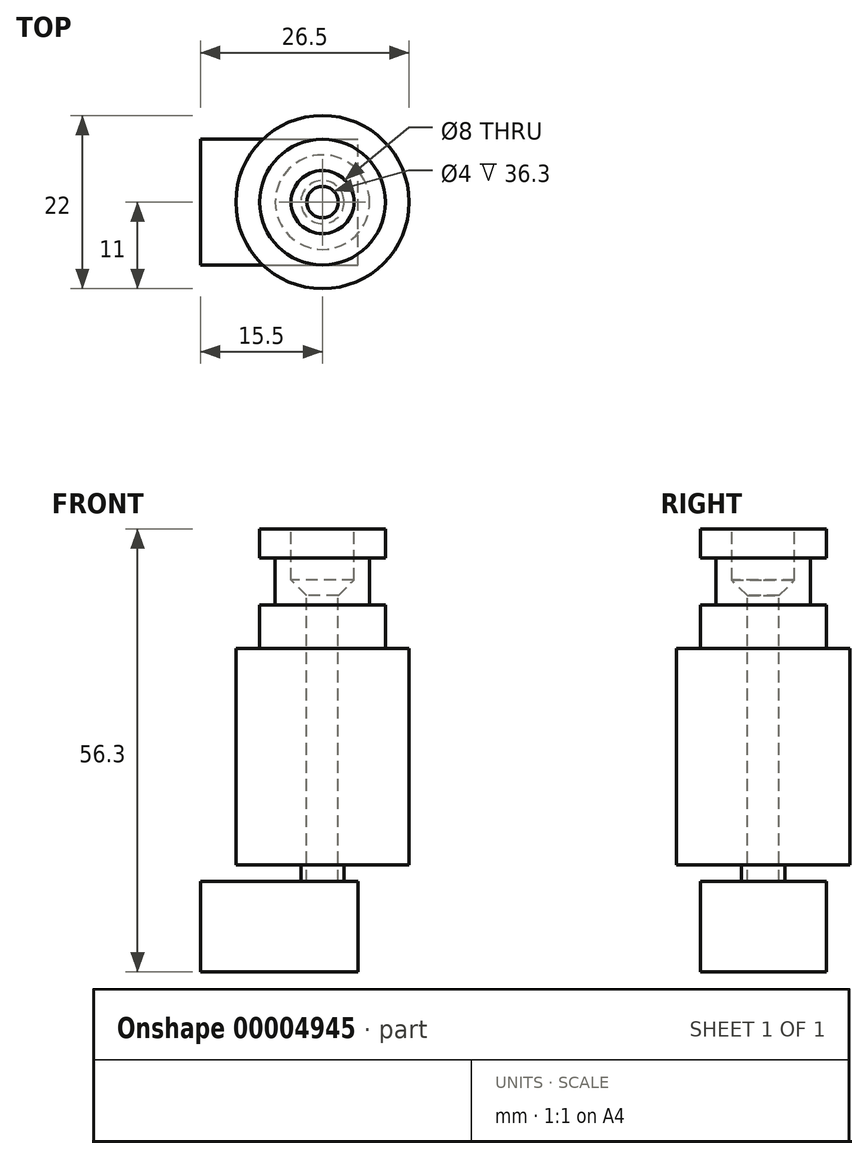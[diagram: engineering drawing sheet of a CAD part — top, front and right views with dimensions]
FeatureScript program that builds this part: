
annotation { "Feature Type Name" : "Feature", "Feature Type Description" : "" }
export const myFeature = defineFeature(function(context is Context, id is Id, definition is map)
    precondition{}
    {
        {
            var Q0;
            Q0=qCreatedBy(makeId("Front.planeOp"),FACE);
            var sketch = newSketch(context, id + "F0", { "sketchPlane" : qUnion([Q0])});
            skLineSegment(sketch, "E0", {"start": v(0, 0) * mm, "end": v(0, -42.7) * mm, "construction": true});
            skLineSegment(sketch, "E1", {"start": v(4, 0) * mm, "end": v(4, -6.5) * mm});
            skLineSegment(sketch, "E2", {"start": v(4, -6.5) * mm, "end": v(2, -8.5) * mm});
            skLineSegment(sketch, "E3", {"start": v(2, -8.5) * mm, "end": v(2, -42.7) * mm});
            skLineSegment(sketch, "E4", {"start": v(2, -42.7) * mm, "end": v(2, -49.8) * mm});
            skLineSegment(sketch, "E5", {"start": v(2, -49.8) * mm, "end": v(3, -49.8) * mm});
            skLineSegment(sketch, "E6", {"start": v(3, -49.8) * mm, "end": v(3, -44.8) * mm});
            skLineSegment(sketch, "E7", {"start": v(3, -44.8) * mm, "end": v(2.75, -44.8) * mm});
            skLineSegment(sketch, "E8", {"start": v(2.75, -44.8) * mm, "end": v(2.75, -42.7) * mm});
            skLineSegment(sketch, "E9", {"start": v(2.75, -42.7) * mm, "end": v(11, -42.7) * mm});
            skLineSegment(sketch, "E10", {"start": v(11, -42.7) * mm, "end": v(11, -15.2) * mm});
            skLineSegment(sketch, "E11", {"start": v(4, 0) * mm, "end": v(8, 0) * mm});
            skLineSegment(sketch, "E12", {"start": v(8, 0) * mm, "end": v(8, -3.7) * mm});
            skLineSegment(sketch, "E13", {"start": v(8, -3.7) * mm, "end": v(6, -3.7) * mm});
            skLineSegment(sketch, "E14", {"start": v(6, -3.7) * mm, "end": v(6, -9.7) * mm});
            skLineSegment(sketch, "E15", {"start": v(6, -9.7) * mm, "end": v(8, -9.7) * mm});
            skLineSegment(sketch, "E16", {"start": v(8, -9.7) * mm, "end": v(8, -15.2) * mm});
            skLineSegment(sketch, "E17", {"start": v(8, -15.2) * mm, "end": v(11, -15.2) * mm});
            skSolve(sketch);
        }
        {
            var Q0;
            Q0 = qSketchRegion(id + "F0", true);
            var Q1;
            Q1=sQuery(id+"F0.wireOp",EDGE,"E0");
            revolve(context, id + "F1", {"entities" : qUnion([Q0]), "axis" : qUnion([Q1]), "revolveType" : RevolveType.FULL});
        }
        {
            var Q0;
            Q0=makeQuery(id+"F1.opRevolve","SWEPT_FACE",FACE,{"disambiguationData":[OSD([sQuery(id+"F0.wireOp",EDGE,"E7")])]});
            var sketch = newSketch(context, id + "F2", { "sketchPlane" : qUnion([Q0])});
            skCircle(sketch, "E18.0", {"center": v(0, 0) * mm, "radius": 2.75 * mm, "construction": true});
            skLineSegment(sketch, "E19.bottom", {"start": v(-15.5, -8) * mm, "end": v(4.5, -8) * mm});
            skLineSegment(sketch, "E19.top", {"start": v(-15.5, 8) * mm, "end": v(4.5, 8) * mm});
            skLineSegment(sketch, "E19.left", {"start": v(-15.5, -8) * mm, "end": v(-15.5, 8) * mm});
            skLineSegment(sketch, "E19.right", {"start": v(4.5, -8) * mm, "end": v(4.5, 8) * mm});
            skLineSegment(sketch, "E20", {"start": v(0, 0) * mm, "end": v(4.5, 0) * mm, "construction": true});
            skSolve(sketch);
        }
        {
            var Q0;
            Q0 = qSketchRegion(id + "F2", true);
            extrude(context, id + "F3", {"entities" : qUnion([Q0]), "operationType" : NewBodyOperationType.ADD, "oppositeDirection" : true, "depth" : 11.5 * mm});
        }
    });
